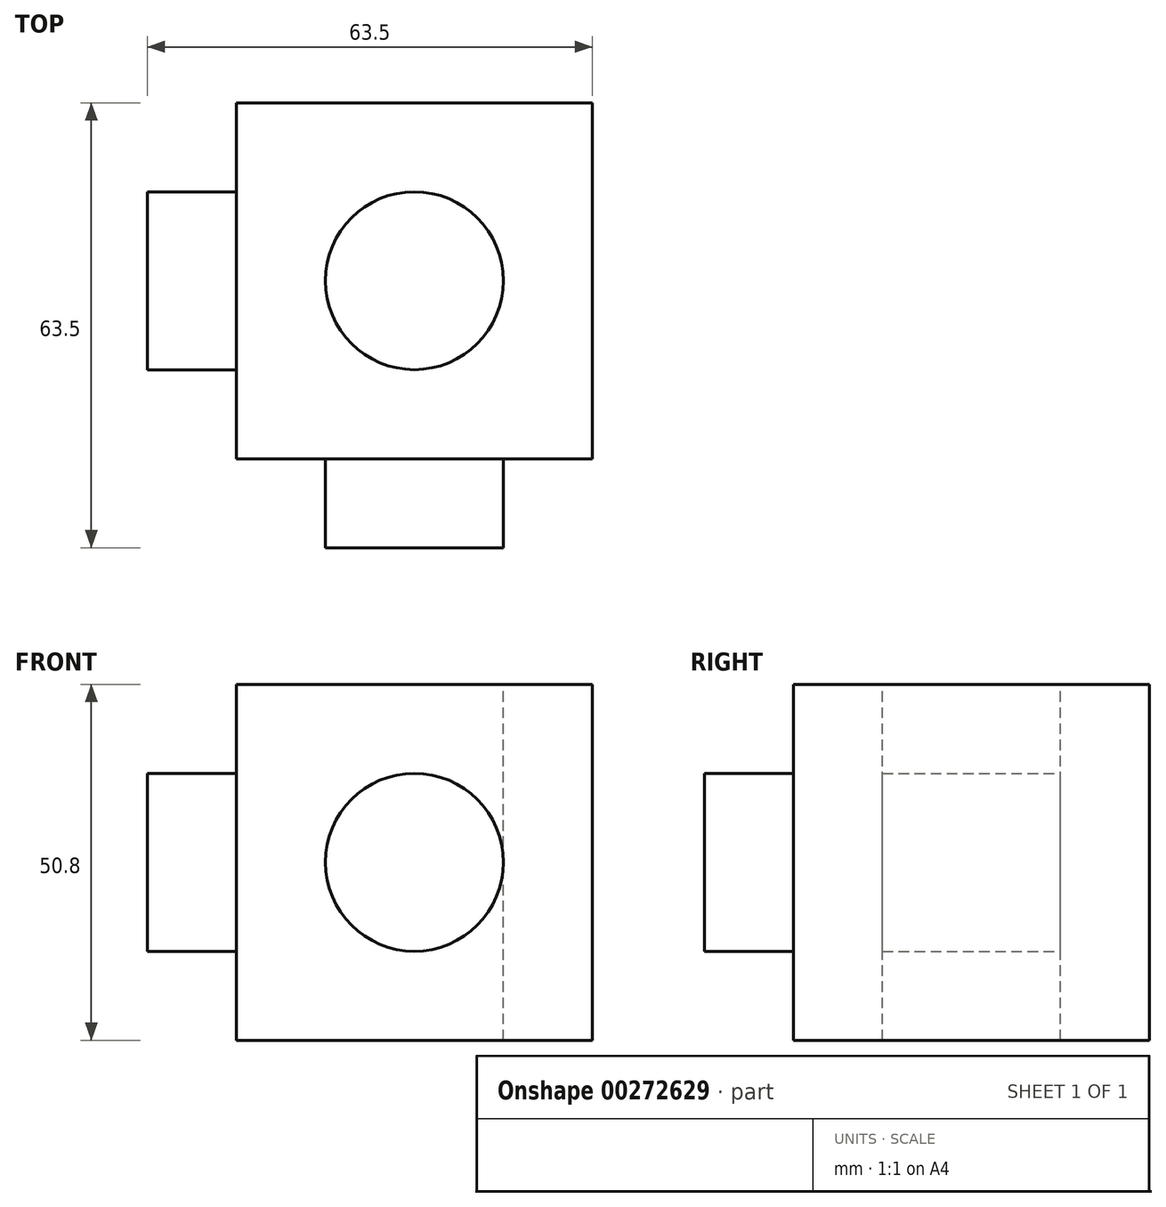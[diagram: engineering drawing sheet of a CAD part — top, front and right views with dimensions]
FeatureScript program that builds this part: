
annotation { "Feature Type Name" : "Feature", "Feature Type Description" : "" }
export const myFeature = defineFeature(function(context is Context, id is Id, definition is map)
    precondition{}
    {
        {
            var Q0;
            Q0=qCreatedBy(makeId("Front.planeOp"),FACE);
            var sketch = newSketch(context, id + "F0", { "sketchPlane" : qUnion([Q0])});
            skLineSegment(sketch, "E0.bottom", {"start": v(0, 0) * mm, "end": v(-50.8, 0) * mm});
            skLineSegment(sketch, "E0.top", {"start": v(0, 50.8) * mm, "end": v(-50.8, 50.8) * mm});
            skLineSegment(sketch, "E0.left", {"start": v(0, 0) * mm, "end": v(0, 50.8) * mm});
            skLineSegment(sketch, "E0.right", {"start": v(-50.8, 0) * mm, "end": v(-50.8, 50.8) * mm});
            skSolve(sketch);
        }
        {
            var Q0;
            Q0 = qSketchRegion(id + "F0", true);
            extrude(context, id + "F1", {"entities" : qUnion([Q0]), "depth" : 50.8 * mm});
        }
        {
            var Q0;
            Q0=makeQuery(id+"F1.opExtrude","SWEPT_FACE",FACE,{"disambiguationData":[OSD([sQuery(id+"F0.wireOp",EDGE,"E0.top")])]});
            var sketch = newSketch(context, id + "F2", { "sketchPlane" : qUnion([Q0])});
            skCircle(sketch, "E1", {"center": v(-25.4, -25.4) * mm, "radius": 12.7 * mm});
            skSolve(sketch);
        }
        {
            var Q0;
            Q0 = qSketchRegion(id + "F2", true);
            extrude(context, id + "F3", {"entities" : qUnion([Q0]), "operationType" : NewBodyOperationType.REMOVE, "oppositeDirection" : true, "depth" : 50.8 * mm});
        }
        {
            var Q0;
            Q0=makeQuery(id+"F1.opExtrude","SWEPT_FACE",FACE,{"disambiguationData":[OSD([sQuery(id+"F0.wireOp",EDGE,"E0.right")])]});
            var sketch = newSketch(context, id + "F4", { "sketchPlane" : qUnion([Q0])});
            skLineSegment(sketch, "E2.bottom", {"start": v(38.1, 12.7) * mm, "end": v(12.7, 12.7) * mm});
            skLineSegment(sketch, "E2.top", {"start": v(38.1, 38.1) * mm, "end": v(12.7, 38.1) * mm});
            skLineSegment(sketch, "E2.left", {"start": v(38.1, 12.7) * mm, "end": v(38.1, 38.1) * mm});
            skLineSegment(sketch, "E2.right", {"start": v(12.7, 12.7) * mm, "end": v(12.7, 38.1) * mm});
            skSolve(sketch);
        }
        {
            var Q0;
            Q0 = qSketchRegion(id + "F4", true);
            extrude(context, id + "F5", {"entities" : qUnion([Q0]), "operationType" : NewBodyOperationType.ADD, "depth" : 12.7 * mm});
        }
        {
            var Q0;
            Q0=makeQuery(id+"F1.opExtrude","CAP_FACE",FACE,{"disambiguationData":[OSD([sQuery(id+"F0.wireOp",EDGE,"E0.bottom"),sQuery(id+"F0.wireOp",EDGE,"E0.top"),sQuery(id+"F0.wireOp",EDGE,"E0.left"),sQuery(id+"F0.wireOp",EDGE,"E0.right")])],"isStart":false});
            var sketch = newSketch(context, id + "F6", { "sketchPlane" : qUnion([Q0])});
            skCircle(sketch, "E3", {"center": v(-25.4, 25.4) * mm, "radius": 12.7 * mm});
            skSolve(sketch);
        }
        {
            var Q0;
            Q0 = qSketchRegion(id + "F6", true);
            extrude(context, id + "F7", {"entities" : qUnion([Q0]), "operationType" : NewBodyOperationType.ADD, "depth" : 12.7 * mm});
        }
    });
